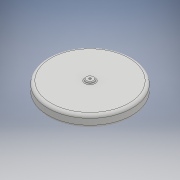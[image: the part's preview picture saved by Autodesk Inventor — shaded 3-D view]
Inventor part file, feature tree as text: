
AUTODESK INVENTOR PART (.ipt)
format: ipt  version: 2018 (Build 220112000, 112)  size: 164,864 bytes
history: native  units: mm
features: sketch x6, fillet x4, extrude x3, hole x2, other x1
ambient origin geometry x8: Origin, YZ Plane, XZ Plane, XY Plane, X Axis, Y Axis, Z Axis, Center Point
bodies: Body1 (feature_tree)
feature tree (16):
  other  "ソリッド1"
  extrude  "押し出し1"  Depth=490.0mm
  fillet  "フィレット1"  Radius=70.0mm
  sketch  "スケッチ4"
  extrude  "押し出し2"  Depth=17.5mm
  extrude  "押し出し3"  Depth=50.0mm
  fillet  "フィレット2"  Radius=10.0mm
  fillet  "フィレット3"  Radius=240.0mm
  fillet  "フィレット4"  Radius=35.0mm
  hole  "穴2"  [1 undecoded]
  hole  "穴3"  [1 undecoded]
  sketch  "スケッチ1"
  sketch  "スケッチ8"
  sketch  "スケッチ9"
  sketch  "スケッチ10"
  sketch  "スケッチ11"
note: 2 required parameter values undecoded (feature->parameter linkage not recoverable at this tier; creation-order binding heuristic only, values carry confidence <= 0.55)
